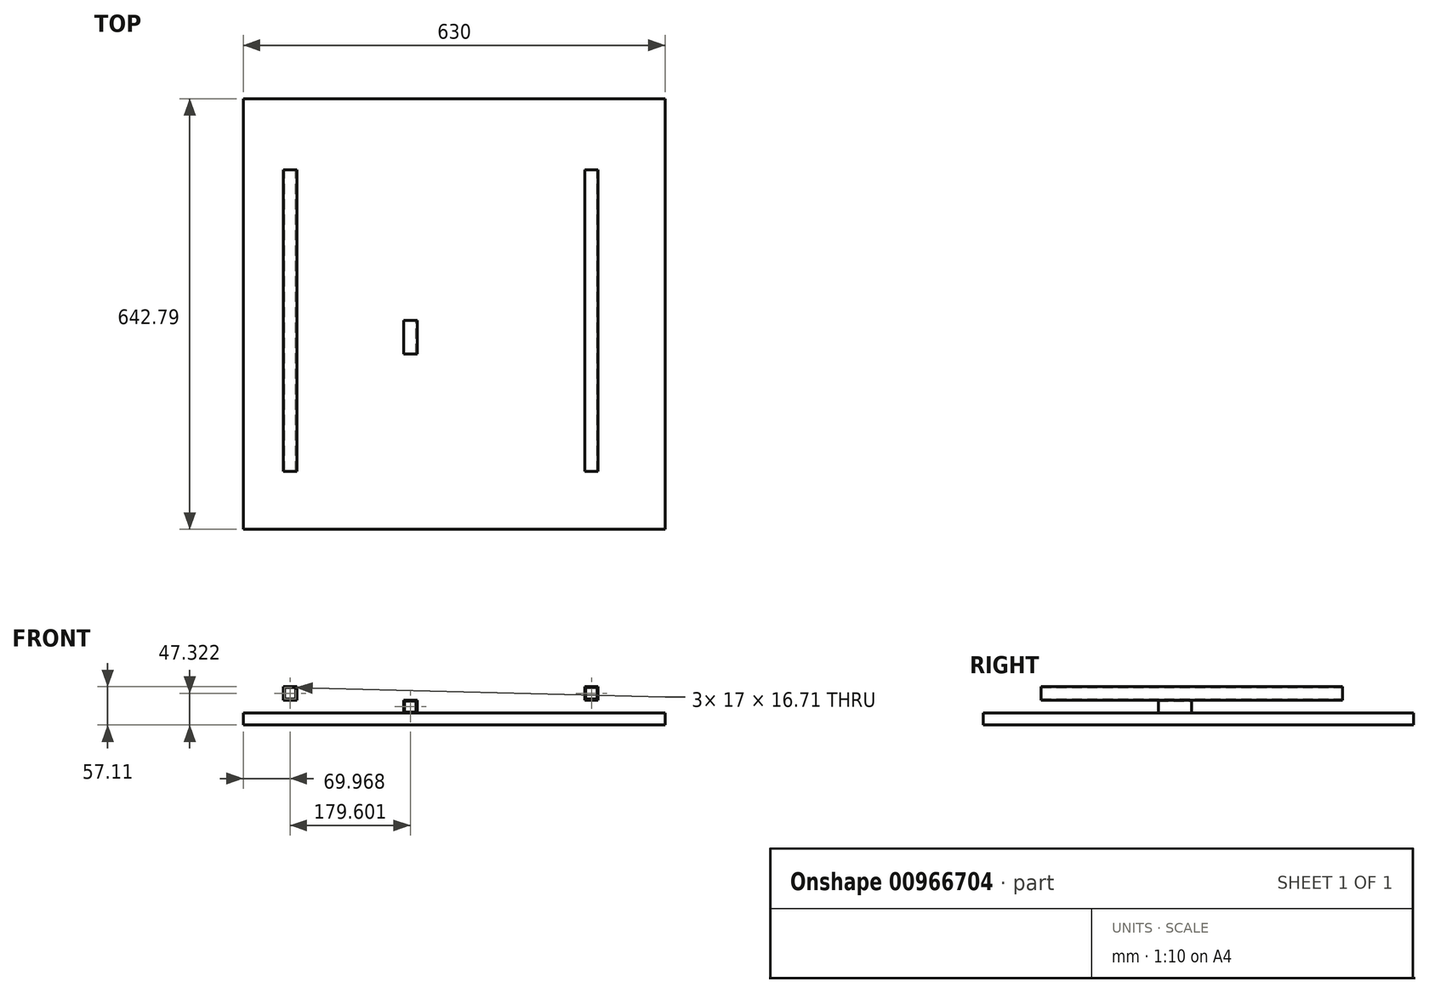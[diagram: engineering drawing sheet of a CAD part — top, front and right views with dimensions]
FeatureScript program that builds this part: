
annotation { "Feature Type Name" : "Feature", "Feature Type Description" : "" }
export const myFeature = defineFeature(function(context is Context, id is Id, definition is map)
    precondition{}
    {
        {
            var Q0;
            Q0=qCreatedBy(makeId("Top.planeOp"),FACE);
            var sketch = newSketch(context, id + "F0", { "sketchPlane" : qUnion([Q0])});
            skLineSegment(sketch, "E0.bottom", {"start": v(-306.83, 331.11) * mm, "end": v(323.17, 331.11) * mm});
            skLineSegment(sketch, "E0.top", {"start": v(-306.83, -311.68) * mm, "end": v(323.17, -311.68) * mm});
            skLineSegment(sketch, "E0.left", {"start": v(-306.83, 331.11) * mm, "end": v(-306.83, -311.68) * mm});
            skLineSegment(sketch, "E0.right", {"start": v(323.17, 331.11) * mm, "end": v(323.17, -311.68) * mm});
            skSolve(sketch);
        }
        {
            var Q0;
            Q0 = qSketchRegion(id + "F0", true);
            extrude(context, id + "F1", {"entities" : qUnion([Q0]), "depth" : 18 * mm, "offsetDistance" : 25.4 * mm});
        }
        {
            var Q0;
            Q0=qCreatedBy(makeId("Front.planeOp"),FACE);
            var sketch = newSketch(context, id + "F2", { "sketchPlane" : qUnion([Q0])});
            skLineSegment(sketch, "E1.bottom", {"start": v(-21.86, 37.1) * mm, "end": v(-1.86, 37.1) * mm});
            skLineSegment(sketch, "E1.top", {"start": v(-21.86, 17.1) * mm, "end": v(-1.86, 17.1) * mm});
            skLineSegment(sketch, "E1.left", {"start": v(-21.86, 37.1) * mm, "end": v(-21.86, 17.1) * mm});
            skLineSegment(sketch, "E1.right", {"start": v(-1.86, 37.1) * mm, "end": v(-1.86, 17.1) * mm});
            skLineSegment(sketch, "E2.bottom", {"start": v(-20.36, 35.68) * mm, "end": v(-3.36, 35.68) * mm});
            skLineSegment(sketch, "E2.top", {"start": v(-20.36, 18.97) * mm, "end": v(-3.36, 18.97) * mm});
            skLineSegment(sketch, "E2.left", {"start": v(-20.36, 35.68) * mm, "end": v(-20.36, 18.97) * mm});
            skLineSegment(sketch, "E2.right", {"start": v(-3.36, 35.68) * mm, "end": v(-3.36, 18.97) * mm});
            skSolve(sketch);
        }
        {
            var Q0;
            Q0=makeQuery(id+"F2.imprint","IMPRINT",FACE,{"disambiguationData":[TD([[makeQuery(id+"F2.imprint","IMPRINT",EDGE,{"derivedFrom":sQuery(id+"F2.wireOp",EDGE,"E1.bottom")}),-1.0]])]});
            extrude(context, id + "F3", {"entities" : qUnion([Q0]), "depth" : 450 * mm, "offsetDistance" : 25 * mm});
        }
        {
            var Q0;
            Q0=makeQuery(id+"F3.opExtrude","SWEPT_BODY",BODY,{"disambiguationData":[OSD([sQuery(id+"F2.wireOp",EDGE,"E1.bottom"),sQuery(id+"F2.wireOp",EDGE,"E1.top"),sQuery(id+"F2.wireOp",EDGE,"E1.left"),sQuery(id+"F2.wireOp",EDGE,"E1.right"),sQuery(id+"F2.wireOp",EDGE,"E2.bottom"),sQuery(id+"F2.wireOp",EDGE,"E2.top"),sQuery(id+"F2.wireOp",EDGE,"E2.left"),sQuery(id+"F2.wireOp",EDGE,"E2.right")])]});
            transform(context, id + "F4", {"entities" : qUnion([Q0]), "transformType" : TransformType.TRANSLATION_3D, "dx" : -225 * mm, "dy" : 225 * mm, "dz" : 20 * mm, "makeCopy" : true});
        }
        {
            var Q0;
            Q0=makeQuery(id+"F3.opExtrude","SWEPT_BODY",BODY,{"disambiguationData":[OSD([sQuery(id+"F2.wireOp",EDGE,"E1.bottom"),sQuery(id+"F2.wireOp",EDGE,"E1.top"),sQuery(id+"F2.wireOp",EDGE,"E1.left"),sQuery(id+"F2.wireOp",EDGE,"E1.right"),sQuery(id+"F2.wireOp",EDGE,"E2.bottom"),sQuery(id+"F2.wireOp",EDGE,"E2.top"),sQuery(id+"F2.wireOp",EDGE,"E2.left"),sQuery(id+"F2.wireOp",EDGE,"E2.right")])]});
            transform(context, id + "F5", {"entities" : qUnion([Q0]), "transformType" : TransformType.TRANSLATION_3D, "dx" : 225 * mm, "dy" : 225 * mm, "dz" : 20 * mm, "makeCopy" : false});
        }
        {
            var Q0;
            Q0=qCreatedBy(makeId("Front.planeOp"),FACE);
            var sketch = newSketch(context, id + "F6", { "sketchPlane" : qUnion([Q0])});
            skLineSegment(sketch, "E3.bottom", {"start": v(-67.26, 37.06) * mm, "end": v(-47.26, 37.06) * mm});
            skLineSegment(sketch, "E3.top", {"start": v(-67.26, 17.06) * mm, "end": v(-47.26, 17.06) * mm});
            skLineSegment(sketch, "E3.left", {"start": v(-67.26, 37.06) * mm, "end": v(-67.26, 17.06) * mm});
            skLineSegment(sketch, "E3.right", {"start": v(-47.26, 37.06) * mm, "end": v(-47.26, 17.06) * mm});
            skLineSegment(sketch, "E4.bottom", {"start": v(-65.76, 35.63) * mm, "end": v(-48.76, 35.63) * mm});
            skLineSegment(sketch, "E4.top", {"start": v(-65.76, 18.92) * mm, "end": v(-48.76, 18.92) * mm});
            skLineSegment(sketch, "E4.left", {"start": v(-65.76, 35.63) * mm, "end": v(-65.76, 18.92) * mm});
            skLineSegment(sketch, "E4.right", {"start": v(-48.76, 35.63) * mm, "end": v(-48.76, 18.92) * mm});
            skSolve(sketch);
        }
        {
            var Q0;
            Q0=makeQuery(id+"F6.imprint","IMPRINT",FACE,{"disambiguationData":[TD([[makeQuery(id+"F6.imprint","IMPRINT",EDGE,{"derivedFrom":sQuery(id+"F6.wireOp",EDGE,"E3.bottom")}),-1.0]])]});
            extrude(context, id + "F7", {"entities" : qUnion([Q0]), "depth" : 50 * mm, "offsetDistance" : 25 * mm});
        }
    });
